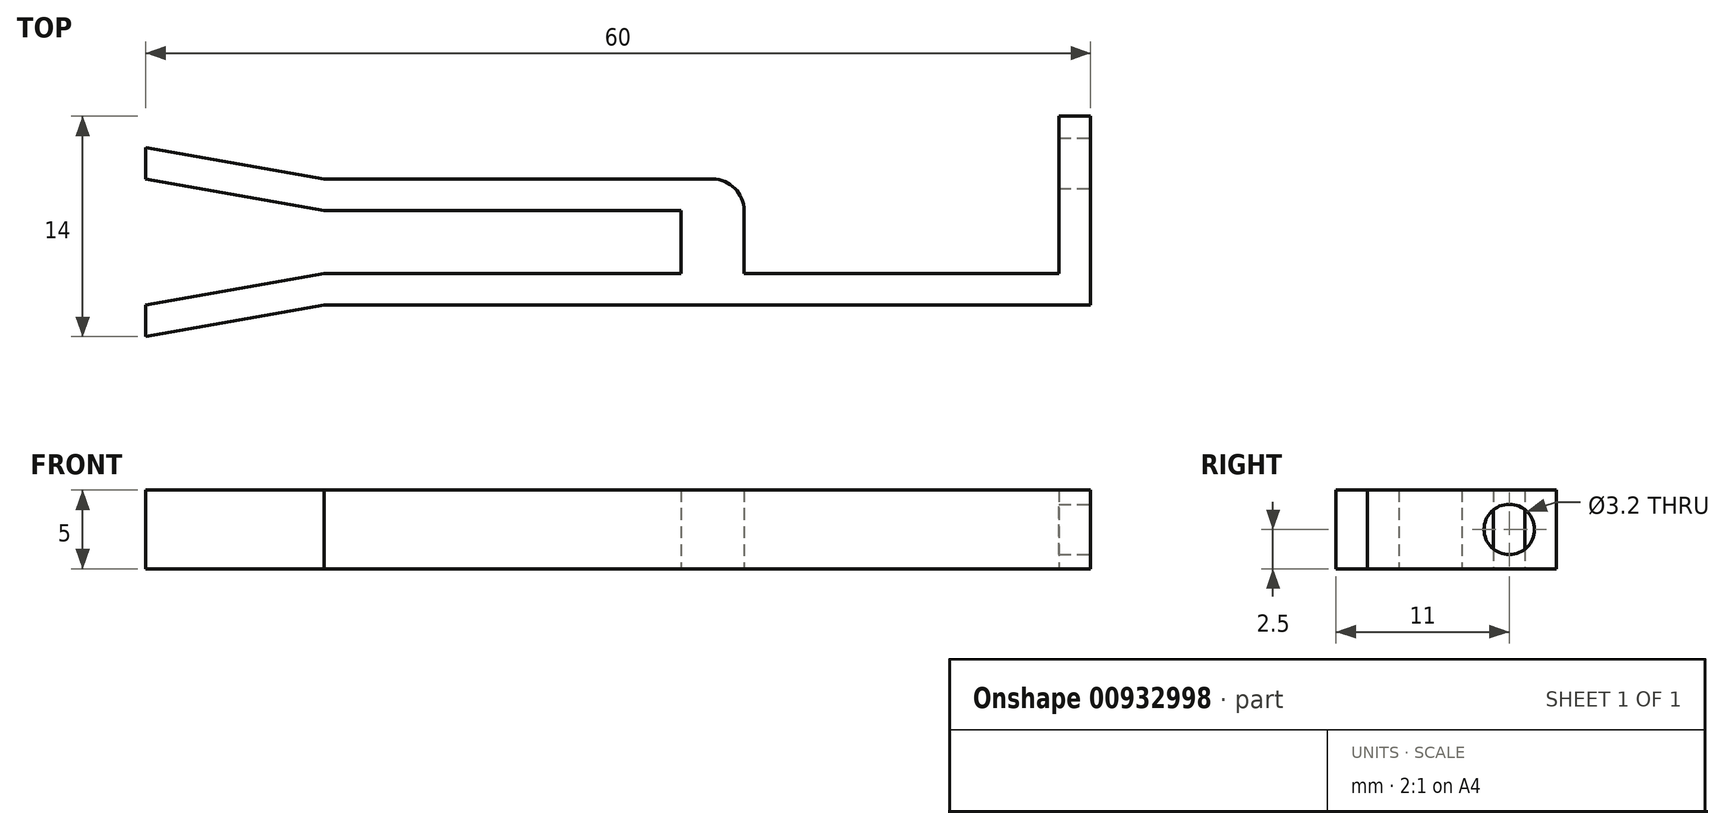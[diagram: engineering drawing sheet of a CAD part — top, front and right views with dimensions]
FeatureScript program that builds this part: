
annotation { "Feature Type Name" : "Feature", "Feature Type Description" : "" }
export const myFeature = defineFeature(function(context is Context, id is Id, definition is map)
    precondition{}
    {
        {
            var Q0;
            Q0=qCreatedBy(makeId("Top.planeOp"),FACE);
            var sketch = newSketch(context, id + "F0", { "sketchPlane" : qUnion([Q0])});
            skLineSegment(sketch, "E0", {"start": v(0, 0) * mm, "end": v(0, 12) * mm});
            skLineSegment(sketch, "E1", {"start": v(-2, 12) * mm, "end": v(-2, 2) * mm});
            skLineSegment(sketch, "E2", {"start": v(-2, 2) * mm, "end": v(-22, 2) * mm});
            skLineSegment(sketch, "E3", {"start": v(-22, 2) * mm, "end": v(-22, 8) * mm});
            skLineSegment(sketch, "E4", {"start": v(-22, 8) * mm, "end": v(-48.66, 8) * mm});
            skLineSegment(sketch, "E5", {"start": v(-48.66, 8) * mm, "end": v(-60, 10) * mm});
            skLineSegment(sketch, "E6", {"start": v(-60, 10) * mm, "end": v(-60, 8) * mm});
            skLineSegment(sketch, "E7", {"start": v(-60, 8) * mm, "end": v(-48.66, 6) * mm});
            skLineSegment(sketch, "E8", {"start": v(-48.66, 6) * mm, "end": v(-26, 6) * mm});
            skLineSegment(sketch, "E9", {"start": v(-26, 6) * mm, "end": v(-26, 2) * mm});
            skLineSegment(sketch, "E10", {"start": v(-26, 2) * mm, "end": v(-48.66, 2) * mm});
            skLineSegment(sketch, "E11", {"start": v(-48.66, 2) * mm, "end": v(-60, 0) * mm});
            skLineSegment(sketch, "E12", {"start": v(-60, 0) * mm, "end": v(-60, -2) * mm});
            skLineSegment(sketch, "E13", {"start": v(-60, -2) * mm, "end": v(-48.66, 0) * mm});
            skLineSegment(sketch, "E14", {"start": v(-48.66, 0) * mm, "end": v(0, 0) * mm});
            skLineSegment(sketch, "E15", {"start": v(-2, 12) * mm, "end": v(0, 12) * mm});
            skSolve(sketch);
        }
        {
            var Q0;
            Q0=makeQuery(id+"F0.imprint","IMPRINT",FACE,{"disambiguationData":[TD([[makeQuery(id+"F0.imprint","IMPRINT",EDGE,{"derivedFrom":sQuery(id+"F0.wireOp",EDGE,"E0")}),1.0]])]});
            extrude(context, id + "F1", {"entities" : qUnion([Q0]), "depth" : 5 * mm, "offsetDistance" : 25 * mm});
        }
        {
            var Q0;
            Q0=makeQuery(id+"F1.opExtrude","SWEPT_FACE",FACE,{"disambiguationData":[OSD([sQuery(id+"F0.wireOp",EDGE,"E0")])]});
            var sketch = newSketch(context, id + "F2", { "sketchPlane" : qUnion([Q0])});
            skCircle(sketch, "E16", {"center": v(9, 2.5) * mm, "radius": 1.6 * mm});
            skSolve(sketch);
        }
        {
            var Q0;
            Q0=makeQuery(id+"F2.imprint","IMPRINT",FACE,{"disambiguationData":[TD([[makeQuery(id+"F2.imprint","IMPRINT",EDGE,{"derivedFrom":sQuery(id+"F2.wireOp",EDGE,"E16")}),1.0]])]});
            extrude(context, id + "F3", {"entities" : qUnion([Q0]), "operationType" : NewBodyOperationType.REMOVE, "oppositeDirection" : true, "depth" : 3 * mm, "offsetDistance" : 25 * mm});
        }
        {
            var Q0;
            Q0=makeQuery(id+"F1.opExtrude","SWEPT_EDGE",EDGE,{"disambiguationData":[OSD([sQuery(id+"F0.wireOp",EDGE,"E3"),sQuery(id+"F0.wireOp",EDGE,"E4")])]});
            fillet(context, id + "F4", {"entities" : qUnion([Q0]), "radius" : 2 * mm, "tangentPropagation" : true, "allowEdgeOverflow" : false});
        }
    });
